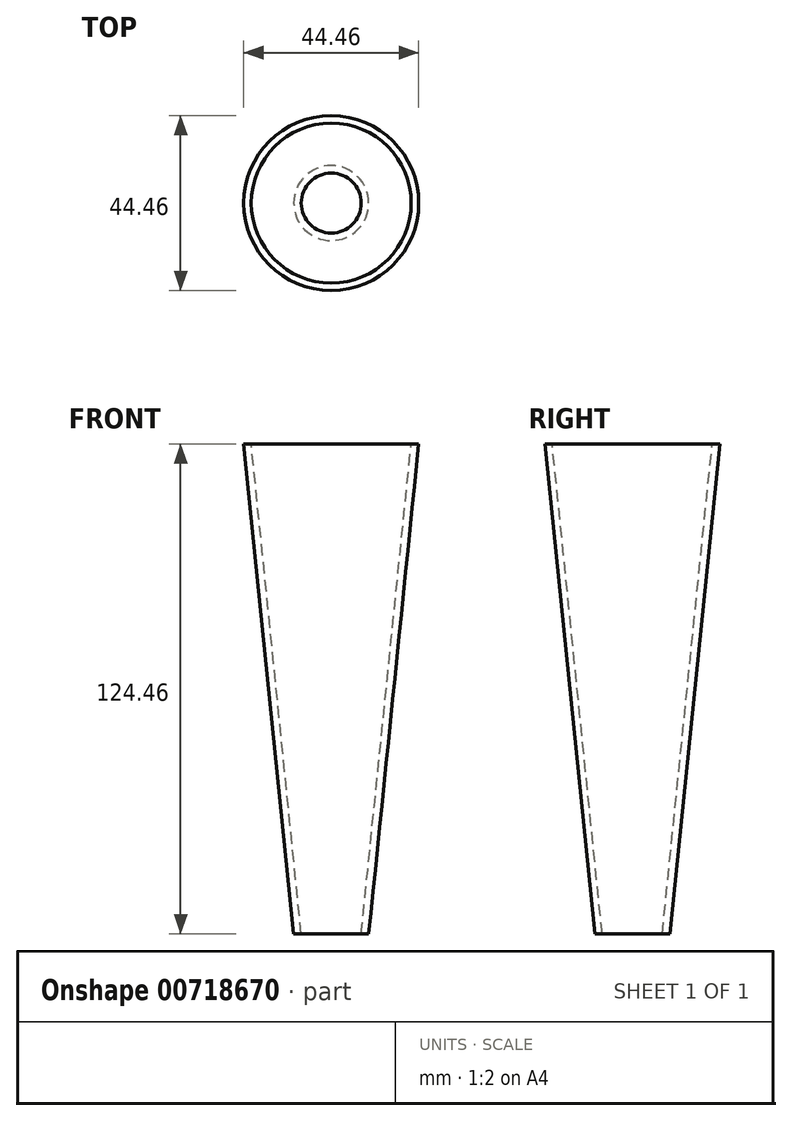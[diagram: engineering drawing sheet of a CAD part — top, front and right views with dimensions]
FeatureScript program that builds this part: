
annotation { "Feature Type Name" : "Feature", "Feature Type Description" : "" }
export const myFeature = defineFeature(function(context is Context, id is Id, definition is map)
    precondition{}
    {
        {
            var Q0;
            Q0=qCreatedBy(makeId("Top.planeOp"),FACE);
            var sketch = newSketch(context, id + "F0", { "sketchPlane" : qUnion([Q0])});
            skCircle(sketch, "E0", {"center": v(0, 0) * mm, "radius": 9.53 * mm});
            skSolve(sketch);
        }
        {
            var Q0;
            Q0=qCreatedBy(makeId("Top.planeOp"),FACE);
            cPlane(context, id + "F1", {"entities" : qUnion([Q0]), "cplaneType" : CPlaneType.OFFSET, "offset" : 124.46 * mm, "width" : 152.4 * mm, "height" : 152.4 * mm});
        }
        {
            var Q0;
            Q0=qCreatedBy(id+"F1.planeOp",FACE);
            var sketch = newSketch(context, id + "F2", { "sketchPlane" : qUnion([Q0])});
            skCircle(sketch, "E1", {"center": v(0, 0) * mm, "radius": 22.23 * mm});
            skSolve(sketch);
        }
        {
            var Q0;
            Q0=makeQuery(id+"F0.imprint","IMPRINT",FACE,{"disambiguationData":[TD([[makeQuery(id+"F0.imprint","IMPRINT",EDGE,{"derivedFrom":sQuery(id+"F0.wireOp",EDGE,"E0")}),1.0]])]});
            var Q1;
            Q1=makeQuery(id+"F2.imprint","IMPRINT",FACE,{"disambiguationData":[TD([[makeQuery(id+"F2.imprint","IMPRINT",EDGE,{"derivedFrom":sQuery(id+"F2.wireOp",EDGE,"E1")}),1.0]])]});
            loft(context, id + "F3", {"sheetProfilesArray" : [{ "sheetProfileEntities" : qUnion([Q0]) }, { "sheetProfileEntities" : qUnion([Q1]) }]});
        }
        {
            var Q0;
            Q0=makeQuery(id+"F3.opLoft","CAP_FACE",FACE,{"disambiguationData":[OSD([makeQuery(id+"F2.imprint","IMPRINT",FACE,{"disambiguationData":[TD([[makeQuery(id+"F2.imprint","IMPRINT",EDGE,{"derivedFrom":sQuery(id+"F2.wireOp",EDGE,"E1")}),1.0]])]})])],"isStart":true});
            var sketch = newSketch(context, id + "F4", { "sketchPlane" : qUnion([Q0])});
            skCircle(sketch, "E2", {"center": v(0, 0) * mm, "radius": 20.32 * mm});
            skSolve(sketch);
        }
        {
            var Q0;
            Q0=makeQuery(id+"F3.opLoft","CAP_FACE",FACE,{"disambiguationData":[OSD([makeQuery(id+"F0.imprint","IMPRINT",FACE,{"disambiguationData":[TD([[makeQuery(id+"F0.imprint","IMPRINT",EDGE,{"derivedFrom":sQuery(id+"F0.wireOp",EDGE,"E0")}),1.0]])]})])],"isStart":true});
            var sketch = newSketch(context, id + "F5", { "sketchPlane" : qUnion([Q0])});
            skCircle(sketch, "E3", {"center": v(0, 0) * mm, "radius": 7.62 * mm});
            skSolve(sketch);
        }
        {
            var Q1;
            Q1=makeQuery(id+"F5.imprint","IMPRINT",FACE,{"disambiguationData":[TD([[makeQuery(id+"F5.imprint","IMPRINT",EDGE,{"derivedFrom":sQuery(id+"F5.wireOp",EDGE,"E3")}),1.0]])]});
            var Q2;
            Q2=makeQuery(id+"F4.imprint","IMPRINT",FACE,{"disambiguationData":[TD([[makeQuery(id+"F4.imprint","IMPRINT",EDGE,{"derivedFrom":sQuery(id+"F4.wireOp",EDGE,"E2")}),1.0]])]});
            loft(context, id + "F6", {"operationType" : NewBodyOperationType.REMOVE, "sheetProfilesArray" : [{ "sheetProfileEntities" : qUnion([Q1]) }, { "sheetProfileEntities" : qUnion([Q2]) }]});
        }
    });
